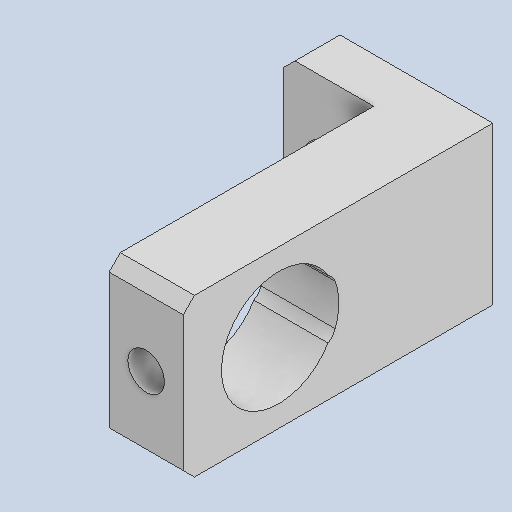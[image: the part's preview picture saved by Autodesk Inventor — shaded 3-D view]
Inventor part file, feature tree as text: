
AUTODESK INVENTOR PART (.ipt)
format: ipt  version: 2024.2 (Build 282272000, 272)  size: 183,808 bytes
history: native  units: in
note: dims shown in document units (in); Inventor stores cm internally (conversion verified against a paired STEP export)
features: extrude x4, hole x1, chamfer x1
ambient origin geometry x8: Origin, YZ Plane, XZ Plane, XY Plane, X Axis, Y Axis, Z Axis, Center Point
bodies: Solid1 (feature_tree)
feature tree (6):
  extrude  "Extrusion1"  Depth=0.2756in
  extrude  "Extrusion3"  Depth=0.1575in
  extrude  "Extrusion2"  Depth=0.1575in TaperAngle=0.0deg
  hole  "Hole2"  [1 undecoded]
  chamfer  "Chamfer1"  [1 undecoded]
  extrude  "Extrusion4"  Depth=0.2598in
note: 2 required parameter values undecoded (feature->parameter linkage not recoverable at this tier; creation-order binding heuristic only, values carry confidence <= 0.55)
